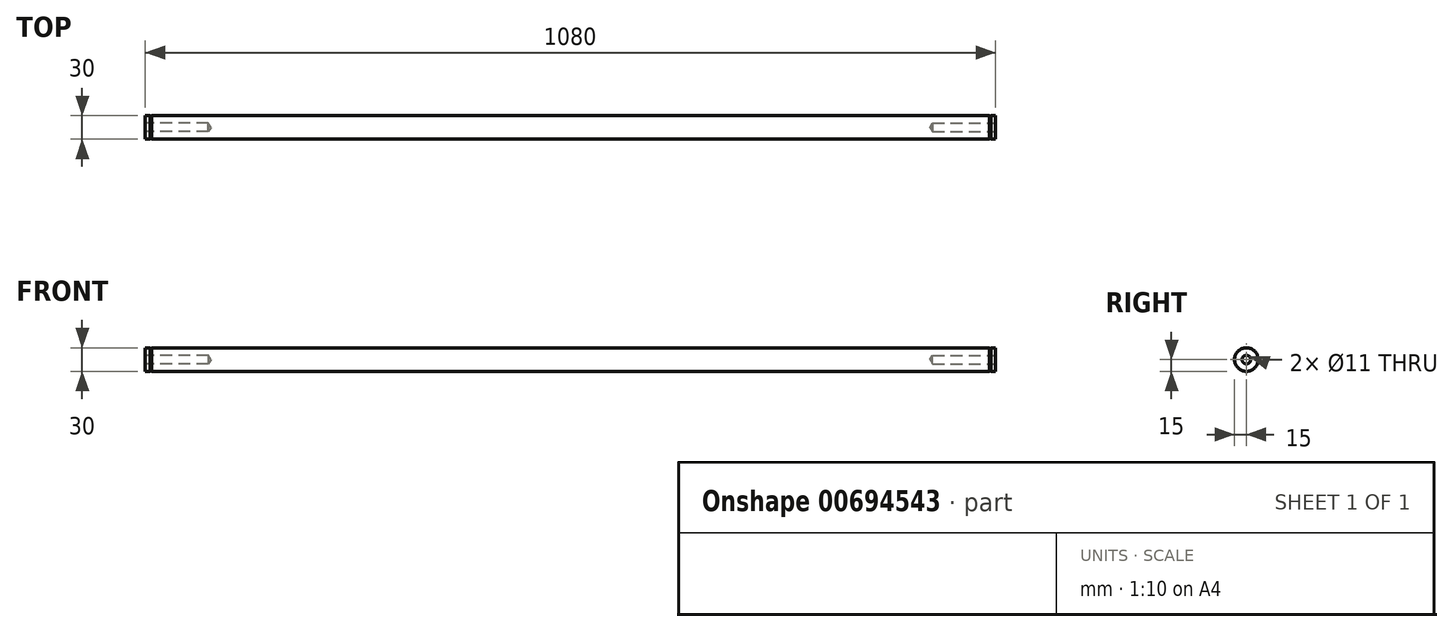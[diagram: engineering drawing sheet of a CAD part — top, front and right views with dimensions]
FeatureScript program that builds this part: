
annotation { "Feature Type Name" : "Feature", "Feature Type Description" : "" }
export const myFeature = defineFeature(function(context is Context, id is Id, definition is map)
    precondition{}
    {
        {
            var Q0;
            Q0=qCreatedBy(makeId("Front.planeOp"),FACE);
            var sketch = newSketch(context, id + "F0", { "sketchPlane" : qUnion([Q0])});
            skLineSegment(sketch, "E0.bottom", {"start": v(-540, 15) * mm, "end": v(-534, 15) * mm});
            skLineSegment(sketch, "E0.top", {"start": v(-540, 0) * mm, "end": v(0, 0) * mm});
            skLineSegment(sketch, "E0.left", {"start": v(-540, 15) * mm, "end": v(-540, 0) * mm});
            skLineSegment(sketch, "E0.right", {"start": v(0, 15) * mm, "end": v(0, 0) * mm});
            skLineSegment(sketch, "E1.bottom", {"start": v(-534, 14.3) * mm, "end": v(-532.3, 14.3) * mm});
            skLineSegment(sketch, "E1.top", {"start": v(-534, 0) * mm, "end": v(-532.3, 0) * mm});
            skLineSegment(sketch, "E1.left", {"start": v(-534, 14.3) * mm, "end": v(-534, 0) * mm});
            skLineSegment(sketch, "E1.right", {"start": v(-532.3, 14.3) * mm, "end": v(-532.3, 0) * mm});
            skLineSegment(sketch, "E2", {"start": v(-534, 15) * mm, "end": v(-534, 14.3) * mm});
            skLineSegment(sketch, "E3", {"start": v(-532.3, 14.3) * mm, "end": v(-532.3, 15) * mm});
            skLineSegment(sketch, "E4.trimOffspring", {"start": v(-532.3, 15) * mm, "end": v(0, 15) * mm});
            skLineSegment(sketch, "E5", {"start": v(6.86, 0) * mm, "end": v(-568.95, 0) * mm, "construction": true});
            skLineSegment(sketch, "E6.MirrorCS", {"start": v(-6.86, 0) * mm, "end": v(568.95, 0) * mm, "construction": true});
            skLineSegment(sketch, "E7.MirrorCS", {"start": v(532.3, 15) * mm, "end": v(0, 15) * mm});
            skLineSegment(sketch, "E8.MirrorCS", {"start": v(534, 14.3) * mm, "end": v(532.3, 14.3) * mm});
            skLineSegment(sketch, "E9.MirrorCS", {"start": v(532.3, 14.3) * mm, "end": v(532.3, 15) * mm});
            skLineSegment(sketch, "E10.MirrorCS", {"start": v(532.3, 14.3) * mm, "end": v(532.3, 0) * mm});
            skLineSegment(sketch, "E11.MirrorCS", {"start": v(534, 14.3) * mm, "end": v(534, 0) * mm});
            skLineSegment(sketch, "E12.MirrorCS", {"start": v(540, 15) * mm, "end": v(534, 15) * mm});
            skLineSegment(sketch, "E13.MirrorCS", {"start": v(534, 15) * mm, "end": v(534, 14.3) * mm});
            skLineSegment(sketch, "E14.MirrorCS", {"start": v(540, 15) * mm, "end": v(540, 0) * mm});
            skLineSegment(sketch, "E15", {"start": v(0, 0) * mm, "end": v(540, 0) * mm});
            skSolve(sketch);
        }
        {
            var Q0;
            {var subQ1=sQuery(id+"F0.wireOp",EDGE,"E11.MirrorCS");Q0=makeQuery(id+"F0.imprint","IMPRINT",FACE,{"disambiguationData":[TD([[makeQuery(id+"F0.imprint","IMPRINT",EDGE,{"derivedFrom":subQ1}),1.0]])]});}
            var Q1;
            Q1=makeQuery(id+"F0.imprint","IMPRINT",FACE,{"disambiguationData":[TD([[makeQuery(id+"F0.imprint","IMPRINT",EDGE,{"derivedFrom":sQuery(id+"F0.wireOp",EDGE,"E8.MirrorCS")}),1.0]])]});
            var Q2;
            {var subQ1=sQuery(id+"F0.wireOp",EDGE,"E0.right");Q2=makeQuery(id+"F0.imprint","IMPRINT",FACE,{"disambiguationData":[TD([[makeQuery(id+"F0.imprint","IMPRINT",EDGE,{"derivedFrom":subQ1}),1.0]])]});}
            var Q3;
            {var subQ1=sQuery(id+"F0.wireOp",EDGE,"E0.right");Q3=makeQuery(id+"F0.imprint","IMPRINT",FACE,{"disambiguationData":[TD([[makeQuery(id+"F0.imprint","IMPRINT",EDGE,{"derivedFrom":subQ1}),-1.0]])]});}
            var Q4;
            Q4=makeQuery(id+"F0.imprint","IMPRINT",FACE,{"disambiguationData":[TD([[makeQuery(id+"F0.imprint","IMPRINT",EDGE,{"derivedFrom":sQuery(id+"F0.wireOp",EDGE,"E1.bottom")}),-1.0]])]});
            var Q5;
            Q5=makeQuery(id+"F0.imprint","IMPRINT",FACE,{"disambiguationData":[TD([[makeQuery(id+"F0.imprint","IMPRINT",EDGE,{"derivedFrom":sQuery(id+"F0.wireOp",EDGE,"E0.bottom")}),-1.0]])]});
            var Q6;
            Q6=sQuery(id+"F0.wireOp",EDGE,"E5");
            revolve(context, id + "F1", {"entities" : qUnion([Q0, Q1, Q2, Q3, Q4, Q5]), "axis" : qUnion([Q6]), "revolveType" : RevolveType.FULL});
        }
        {
            var Q0;
            Q0=makeQuery(id+"F1.opRevolve","SWEPT_FACE",FACE,{"disambiguationData":[OSD([sQuery(id+"F0.wireOp",EDGE,"E0.left")])]});
            var sketch = newSketch(context, id + "F2", { "sketchPlane" : qUnion([Q0])});
            skCircle(sketch, "E16", {"center": v(0, 0) * mm, "radius": 15 * mm});
            skSolve(sketch);
        }
        {
            var Q0;
            Q0=sQuery(id+"F2.wireOp",VERTEX,"E16.center");
            var Q1;
            Q1=makeQuery(id+"F1.opRevolve","SWEPT_BODY",BODY,{"disambiguationData":[OSD([sQuery(id+"F0.wireOp",EDGE,"E0.bottom"),sQuery(id+"F0.wireOp",EDGE,"E0.top"),sQuery(id+"F0.wireOp",EDGE,"E0.left"),sQuery(id+"F0.wireOp",EDGE,"E1.bottom"),sQuery(id+"F0.wireOp",EDGE,"E1.top"),sQuery(id+"F0.wireOp",EDGE,"E2"),sQuery(id+"F0.wireOp",EDGE,"E3"),sQuery(id+"F0.wireOp",EDGE,"E4.trimOffspring"),sQuery(id+"F0.wireOp",EDGE,"E7.MirrorCS"),sQuery(id+"F0.wireOp",EDGE,"E8.MirrorCS"),sQuery(id+"F0.wireOp",EDGE,"E12.MirrorCS"),sQuery(id+"F0.wireOp",EDGE,"E13.MirrorCS"),sQuery(id+"F0.wireOp",EDGE,"E9.MirrorCS"),sQuery(id+"F0.wireOp",EDGE,"E14.MirrorCS"),sQuery(id+"F0.wireOp",EDGE,"E15")])]});
            hole(context, id + "F3", {"style" : HoleStyle.SIMPLE, "endStyle" : HoleEndStyle.BLIND, "standardTappedOrClearance" : lookupTablePath({ "standard" : "ISO", "fit" : "Normal", "size" : "M10", "type" : "Clearance" }), "standardBlindInLast" : lookupTablePath({ "fit" : "Standard", "standard" : "ISO", "size" : "M10", "type" : "Clearance" }), "holeDiameter" : 11 * mm, "majorDiameter" : 8 * mm, "holeDepth" : 80 * mm, "isTappedThrough" : true, "tappedDepth" : 15 * mm, "tapClearance" : 3, "startFromSketch" : true, "locations" : qUnion([Q0]), "scope" : qUnion([Q1])});
        }
        {
            var Q0;
            Q0=makeQuery(id+"F1.opRevolve","SWEPT_FACE",FACE,{"disambiguationData":[OSD([sQuery(id+"F0.wireOp",EDGE,"E14.MirrorCS")])]});
            var sketch = newSketch(context, id + "F4", { "sketchPlane" : qUnion([Q0])});
            skCircle(sketch, "E17", {"center": v(0, 0) * mm, "radius": 15 * mm});
            skSolve(sketch);
        }
        {
            var Q0;
            Q0=sQuery(id+"F4.wireOp",VERTEX,"E17.center");
            var Q1;
            Q1=makeQuery(id+"F1.opRevolve","SWEPT_BODY",BODY,{"disambiguationData":[OSD([sQuery(id+"F0.wireOp",EDGE,"E0.bottom"),sQuery(id+"F0.wireOp",EDGE,"E0.top"),sQuery(id+"F0.wireOp",EDGE,"E0.left"),sQuery(id+"F0.wireOp",EDGE,"E1.bottom"),sQuery(id+"F0.wireOp",EDGE,"E1.top"),sQuery(id+"F0.wireOp",EDGE,"E2"),sQuery(id+"F0.wireOp",EDGE,"E3"),sQuery(id+"F0.wireOp",EDGE,"E4.trimOffspring"),sQuery(id+"F0.wireOp",EDGE,"E7.MirrorCS"),sQuery(id+"F0.wireOp",EDGE,"E8.MirrorCS"),sQuery(id+"F0.wireOp",EDGE,"E12.MirrorCS"),sQuery(id+"F0.wireOp",EDGE,"E13.MirrorCS"),sQuery(id+"F0.wireOp",EDGE,"E9.MirrorCS"),sQuery(id+"F0.wireOp",EDGE,"E14.MirrorCS"),sQuery(id+"F0.wireOp",EDGE,"E15")])]});
            hole(context, id + "F5", {"style" : HoleStyle.SIMPLE, "endStyle" : HoleEndStyle.BLIND, "standardTappedOrClearance" : lookupTablePath({ "standard" : "ISO", "fit" : "Normal", "size" : "M10", "type" : "Clearance" }), "standardBlindInLast" : lookupTablePath({ "fit" : "Standard", "standard" : "ISO", "size" : "M10", "type" : "Clearance" }), "holeDiameter" : 11 * mm, "majorDiameter" : 5 * mm, "holeDepth" : 80 * mm, "isTappedThrough" : true, "tappedDepth" : 15 * mm, "tapClearance" : 3, "startFromSketch" : true, "locations" : qUnion([Q0]), "scope" : qUnion([Q1])});
        }
    });
